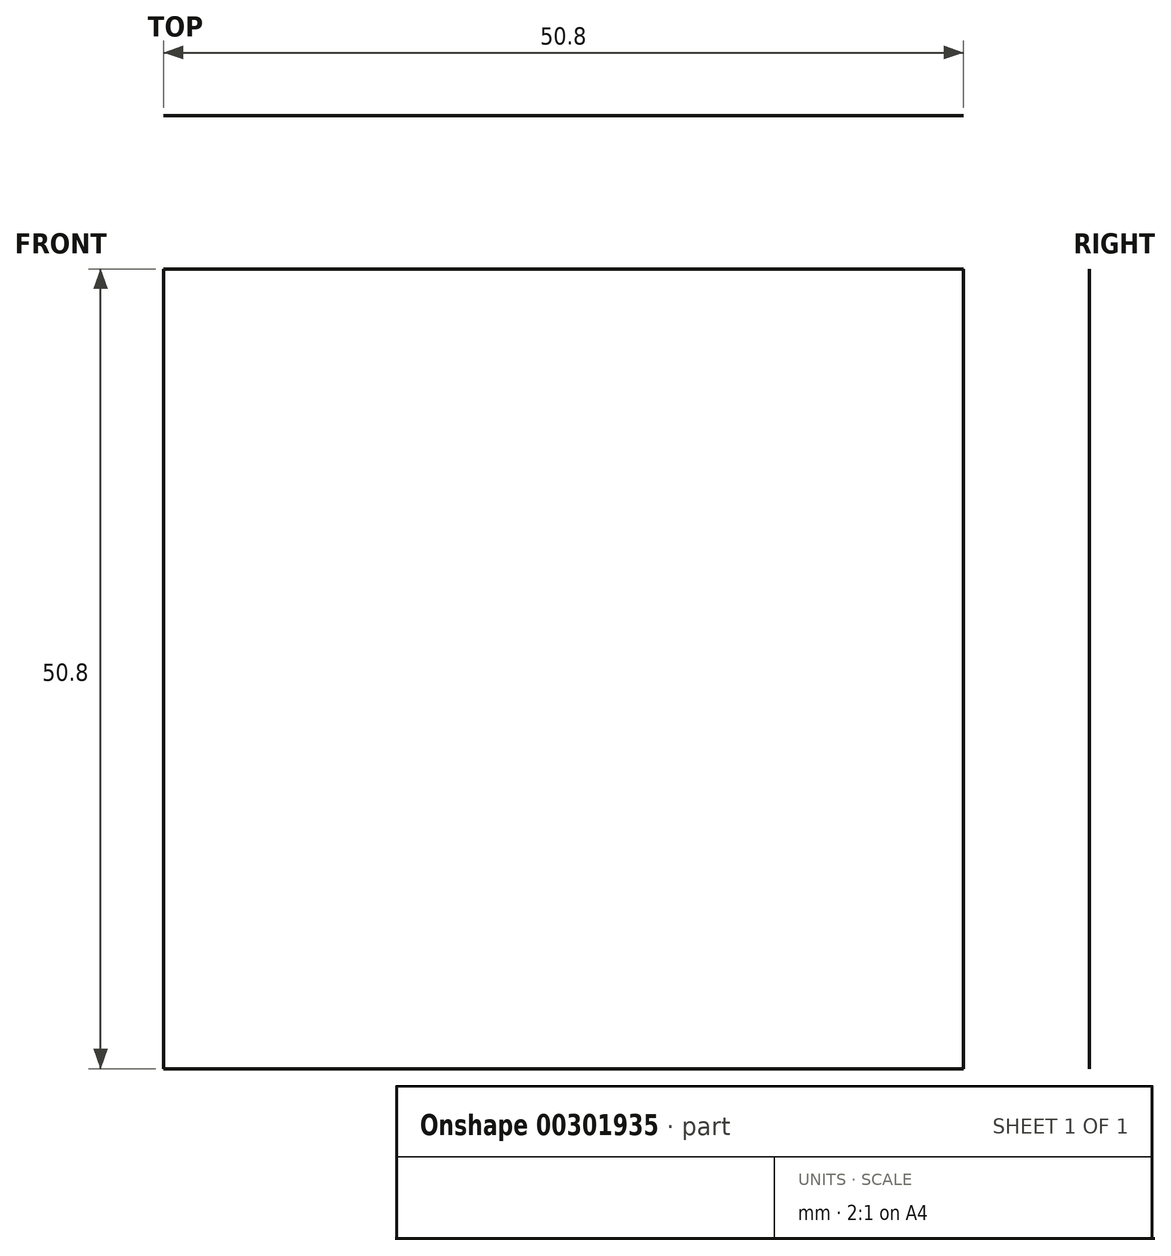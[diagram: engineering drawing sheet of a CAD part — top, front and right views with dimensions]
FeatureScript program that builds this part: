
annotation { "Feature Type Name" : "Feature", "Feature Type Description" : "" }
export const myFeature = defineFeature(function(context is Context, id is Id, definition is map)
    precondition{}
    {
        {
            var Q0;
            Q0=qCreatedBy(makeId("Front.planeOp"),FACE);
            var sketch = newSketch(context, id + "F0", { "sketchPlane" : qUnion([Q0])});
            skLineSegment(sketch, "E0.bottom", {"start": v(-25.4, 25.4) * mm, "end": v(25.4, 25.4) * mm});
            skLineSegment(sketch, "E0.top", {"start": v(-25.4, -25.4) * mm, "end": v(25.4, -25.4) * mm});
            skLineSegment(sketch, "E0.left", {"start": v(-25.4, 25.4) * mm, "end": v(-25.4, -25.4) * mm});
            skLineSegment(sketch, "E0.right", {"start": v(25.4, 25.4) * mm, "end": v(25.4, -25.4) * mm});
            skPoint(sketch, "E0.middle", {"position": v(0, 0) * mm});
            skSolve(sketch);
        }
        {
            var Q0;
            Q0=makeQuery(id+"F0.imprint","IMPRINT",FACE,{"disambiguationData":[TD([[makeQuery(id+"F0.imprint","IMPRINT",EDGE,{"derivedFrom":sQuery(id+"F0.wireOp",EDGE,"E0.bottom")}),-1.0]])]});
            extrude(context, id + "F1", {"entities" : qUnion([Q0]), "depth" : 1 / 203.2 * mm});
        }
    });
